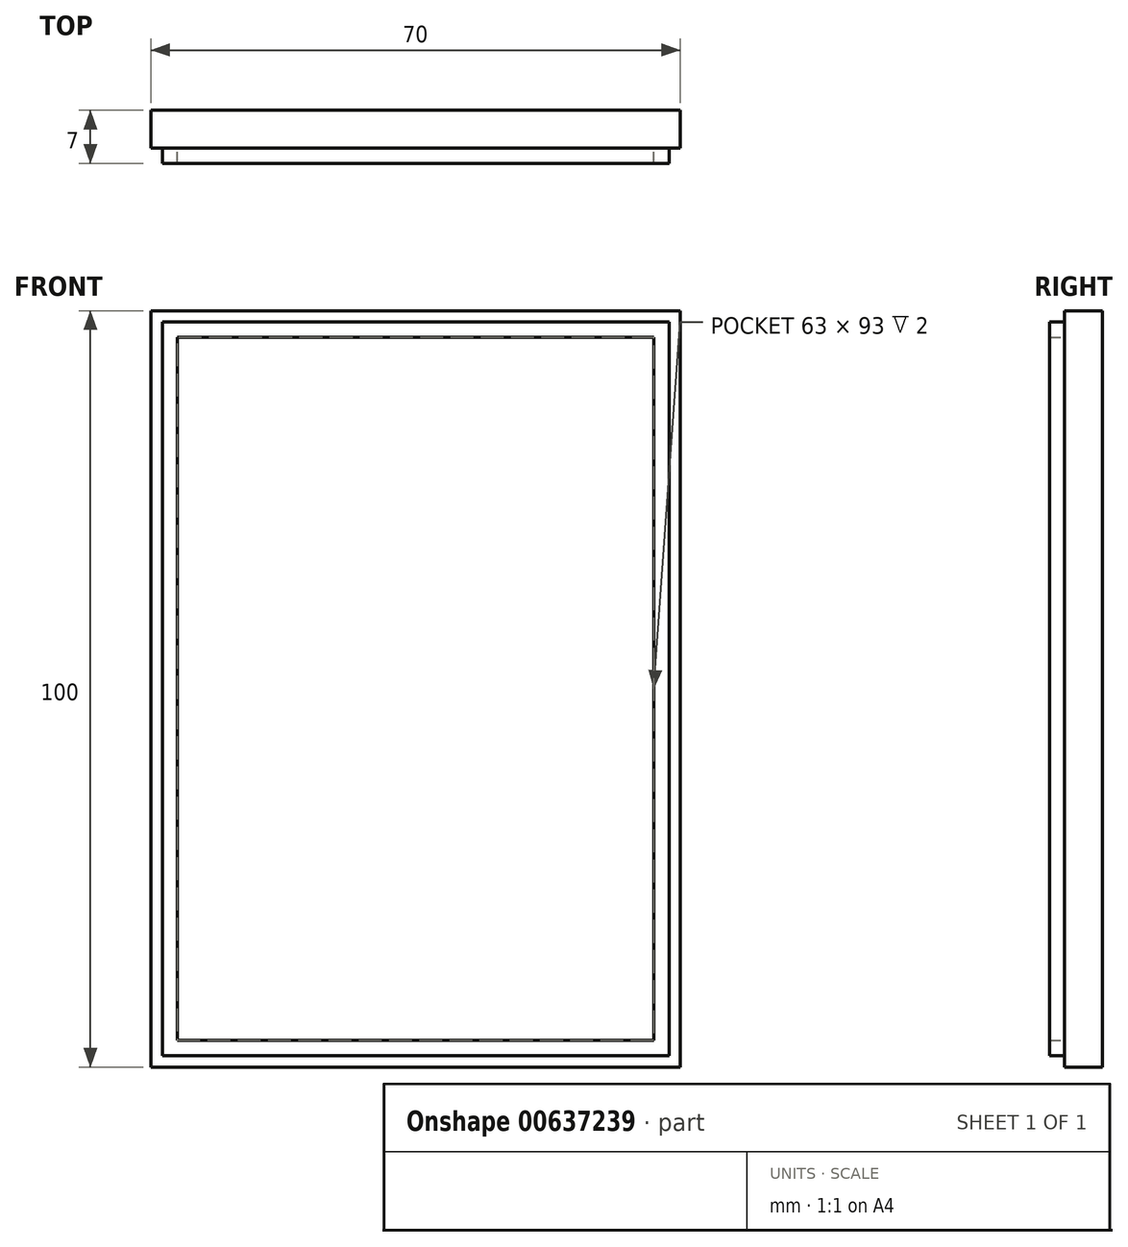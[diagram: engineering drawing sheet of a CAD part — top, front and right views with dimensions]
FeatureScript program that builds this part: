
annotation { "Feature Type Name" : "Feature", "Feature Type Description" : "" }
export const myFeature = defineFeature(function(context is Context, id is Id, definition is map)
    precondition{}
    {
        {
            var Q0;
            Q0=qCreatedBy(makeId("Front.planeOp"),FACE);
            var sketch = newSketch(context, id + "F0", { "sketchPlane" : qUnion([Q0])});
            skLineSegment(sketch, "E0.bottom", {"start": v(-38.94, 64.35) * mm, "end": v(31.06, 64.35) * mm});
            skLineSegment(sketch, "E0.top", {"start": v(-38.94, -35.65) * mm, "end": v(31.06, -35.65) * mm});
            skLineSegment(sketch, "E0.left", {"start": v(-38.94, 64.35) * mm, "end": v(-38.94, -35.65) * mm});
            skLineSegment(sketch, "E0.right", {"start": v(31.06, 64.35) * mm, "end": v(31.06, -35.65) * mm});
            skSolve(sketch);
        }
        {
            var Q0;
            Q0 = qSketchRegion(id + "F0", true);
            extrude(context, id + "F1", {"entities" : qUnion([Q0]), "depth" : 5 * mm, "offsetDistance" : 25 * mm});
        }
        {
            var Q0;
            Q0=makeQuery(id+"F1.opExtrude","CAP_FACE",FACE,{"disambiguationData":[OSD([sQuery(id+"F0.wireOp",EDGE,"E0.bottom"),sQuery(id+"F0.wireOp",EDGE,"E0.top"),sQuery(id+"F0.wireOp",EDGE,"E0.left"),sQuery(id+"F0.wireOp",EDGE,"E0.right")])],"isStart":false});
            var sketch = newSketch(context, id + "F2", { "sketchPlane" : qUnion([Q0])});
            skLineSegment(sketch, "E1.top", {"start": v(-37.44, -34.15) * mm, "end": v(29.56, -34.15) * mm});
            skLineSegment(sketch, "E1.left", {"start": v(-37.44, 62.85) * mm, "end": v(-37.44, -34.15) * mm});
            skLineSegment(sketch, "E2.bottom", {"start": v(-35.44, 60.85) * mm, "end": v(27.56, 60.85) * mm});
            skLineSegment(sketch, "E2.top", {"start": v(-35.44, -32.15) * mm, "end": v(27.56, -32.15) * mm});
            skLineSegment(sketch, "E2.left", {"start": v(-35.44, 60.85) * mm, "end": v(-35.44, -32.15) * mm});
            skLineSegment(sketch, "E2.right", {"start": v(27.56, 60.85) * mm, "end": v(27.56, -32.15) * mm});
            skLineSegment(sketch, "E3", {"start": v(-37.44, 62.85) * mm, "end": v(29.56, 62.85) * mm});
            skLineSegment(sketch, "E4", {"start": v(29.56, 62.85) * mm, "end": v(29.56, -34.15) * mm});
            skSolve(sketch);
        }
        {
            var Q0;
            Q0=makeQuery(id+"F2.imprint","IMPRINT",FACE,{"disambiguationData":[TD([[makeQuery(id+"F2.imprint","IMPRINT",EDGE,{"derivedFrom":sQuery(id+"F2.wireOp",EDGE,"E1.top")}),1.0]])]});
            extrude(context, id + "F3", {"entities" : qUnion([Q0]), "operationType" : NewBodyOperationType.ADD, "depth" : 2 * mm, "offsetDistance" : 25 * mm});
        }
    });
